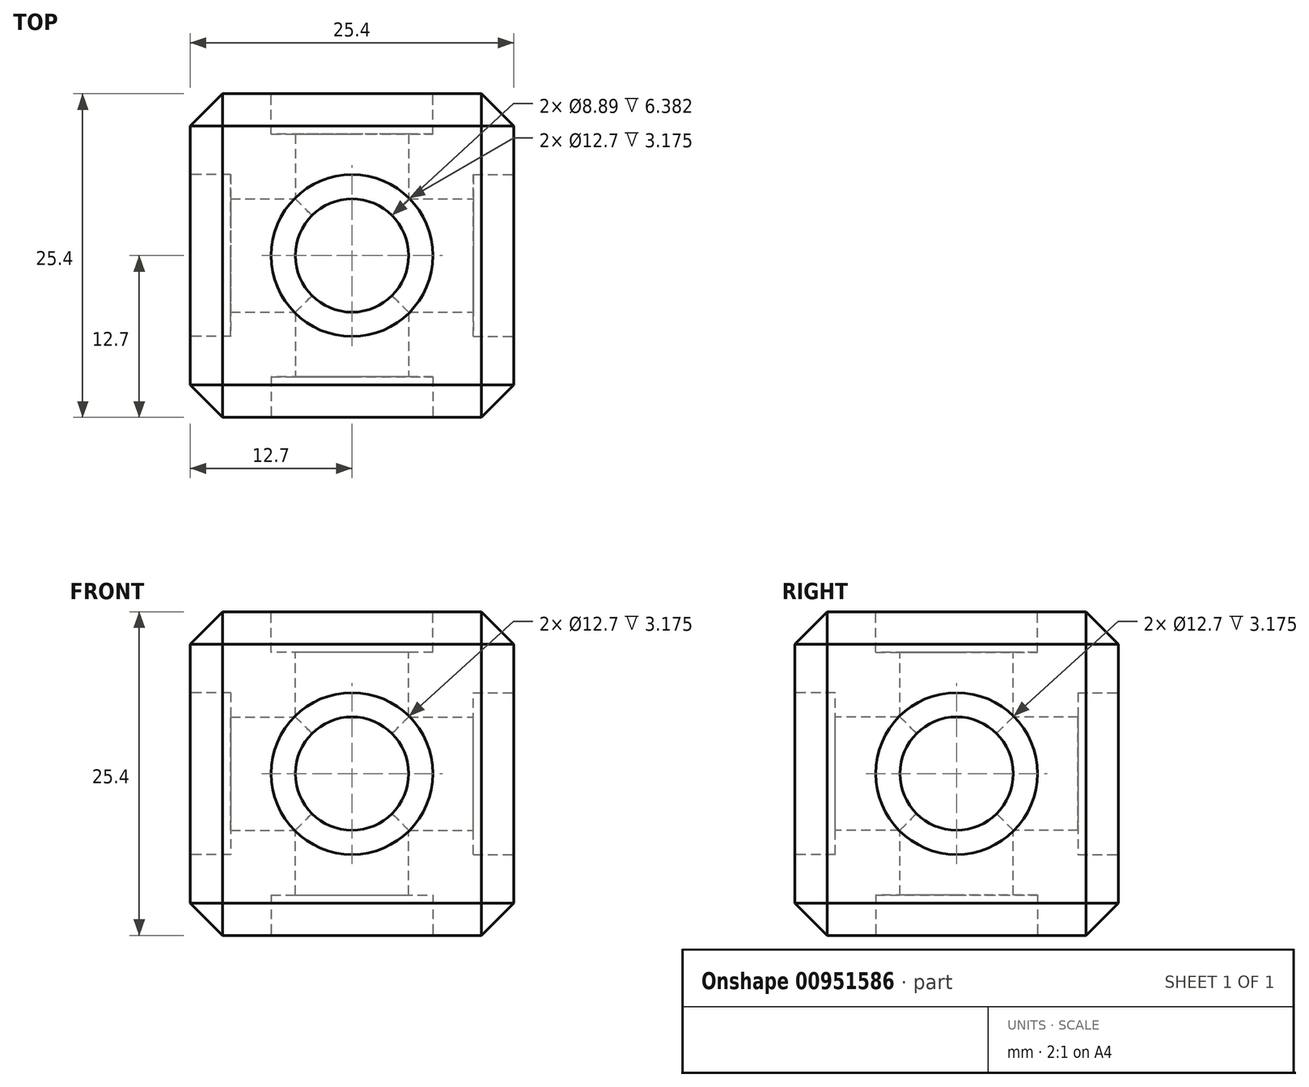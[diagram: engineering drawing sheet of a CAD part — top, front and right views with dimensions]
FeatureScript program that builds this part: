
annotation { "Feature Type Name" : "Feature", "Feature Type Description" : "" }
export const myFeature = defineFeature(function(context is Context, id is Id, definition is map)
    precondition{}
    {
        {
            var Q0;
            Q0=qCreatedBy(makeId("Front.planeOp"),FACE);
            var sketch = newSketch(context, id + "F0", { "sketchPlane" : qUnion([Q0])});
            skLineSegment(sketch, "E0.bottom", {"start": v(12.7, -12.7) * mm, "end": v(-12.7, -12.7) * mm});
            skLineSegment(sketch, "E0.top", {"start": v(12.7, 12.7) * mm, "end": v(-12.7, 12.7) * mm});
            skLineSegment(sketch, "E0.left", {"start": v(12.7, -12.7) * mm, "end": v(12.7, 12.7) * mm});
            skLineSegment(sketch, "E0.right", {"start": v(-12.7, -12.7) * mm, "end": v(-12.7, 12.7) * mm});
            skPoint(sketch, "E0.middle", {"position": v(0, 0) * mm});
            skSolve(sketch);
        }
        {
            var Q0;
            Q0 = qSketchRegion(id + "F0", true);
            extrude(context, id + "F1", {"entities" : qUnion([Q0]), "depth" : 12.7 * mm, "offsetDistance" : 25.4 * mm, "hasSecondDirection" : true, "secondDirectionOppositeDirection" : true, "secondDirectionDepth" : 12.7 * mm});
        }
        {
            var Q0;
            Q0=makeQuery(id+"F1.opExtrude","SWEPT_FACE",FACE,{"disambiguationData":[OSD([sQuery(id+"F0.wireOp",EDGE,"E0.top")])]});
            var sketch = newSketch(context, id + "F2", { "sketchPlane" : qUnion([Q0])});
            skCircle(sketch, "E1", {"center": v(0, 0) * mm, "radius": 6.35 * mm});
            skCircle(sketch, "E2", {"center": v(0, 0) * mm, "radius": 4.45 * mm});
            skSolve(sketch);
        }
        {
            var Q0;
            Q0=makeQuery(id+"F1.opExtrude","SWEPT_FACE",FACE,{"disambiguationData":[OSD([sQuery(id+"F0.wireOp",EDGE,"E0.bottom")])]});
            var sketch = newSketch(context, id + "F3", { "sketchPlane" : qUnion([Q0])});
            skCircle(sketch, "E3", {"center": v(0, 0) * mm, "radius": 6.35 * mm});
            skCircle(sketch, "E4", {"center": v(0, 0) * mm, "radius": 4.45 * mm});
            skSolve(sketch);
        }
        {
            var Q0;
            Q0=makeQuery(id+"F1.opExtrude","CAP_FACE",FACE,{"disambiguationData":[OSD([sQuery(id+"F0.wireOp",EDGE,"E0.bottom"),sQuery(id+"F0.wireOp",EDGE,"E0.top"),sQuery(id+"F0.wireOp",EDGE,"E0.left"),sQuery(id+"F0.wireOp",EDGE,"E0.right")])],"isStart":false});
            var sketch = newSketch(context, id + "F4", { "sketchPlane" : qUnion([Q0])});
            skCircle(sketch, "E5", {"center": v(0, 0) * mm, "radius": 6.35 * mm});
            skCircle(sketch, "E6", {"center": v(0, 0) * mm, "radius": 4.45 * mm});
            skSolve(sketch);
        }
        {
            var Q0;
            Q0=makeQuery(id+"F1.opExtrude","CAP_FACE",FACE,{"disambiguationData":[OSD([sQuery(id+"F0.wireOp",EDGE,"E0.bottom"),sQuery(id+"F0.wireOp",EDGE,"E0.top"),sQuery(id+"F0.wireOp",EDGE,"E0.left"),sQuery(id+"F0.wireOp",EDGE,"E0.right")])],"isStart":true});
            var sketch = newSketch(context, id + "F5", { "sketchPlane" : qUnion([Q0])});
            skCircle(sketch, "E7", {"center": v(0, 0) * mm, "radius": 6.35 * mm});
            skCircle(sketch, "E8", {"center": v(0, 0) * mm, "radius": 4.45 * mm});
            skSolve(sketch);
        }
        {
            var Q0;
            Q0=makeQuery(id+"F1.opExtrude","SWEPT_FACE",FACE,{"disambiguationData":[OSD([sQuery(id+"F0.wireOp",EDGE,"E0.left")])]});
            var sketch = newSketch(context, id + "F6", { "sketchPlane" : qUnion([Q0])});
            skCircle(sketch, "E9", {"center": v(0, 0) * mm, "radius": 6.35 * mm});
            skCircle(sketch, "E10", {"center": v(0, 0) * mm, "radius": 4.45 * mm});
            skSolve(sketch);
        }
        {
            var Q0;
            Q0=makeQuery(id+"F1.opExtrude","SWEPT_FACE",FACE,{"disambiguationData":[OSD([sQuery(id+"F0.wireOp",EDGE,"E0.right")])]});
            var sketch = newSketch(context, id + "F7", { "sketchPlane" : qUnion([Q0])});
            skCircle(sketch, "E11", {"center": v(0, 0) * mm, "radius": 6.35 * mm});
            skCircle(sketch, "E12", {"center": v(0, 0) * mm, "radius": 4.45 * mm});
            skSolve(sketch);
        }
        {
            var Q0;
            Q0=makeQuery(id+"F2.imprint","IMPRINT",FACE,{"disambiguationData":[TD([[makeQuery(id+"F2.imprint","IMPRINT",EDGE,{"derivedFrom":sQuery(id+"F2.wireOp",EDGE,"E2")}),1.0]])]});
            extrude(context, id + "F8", {"entities" : qUnion([Q0]), "operationType" : NewBodyOperationType.REMOVE, "oppositeDirection" : true, "depth" : 25.4 * mm, "offsetDistance" : 25.4 * mm});
        }
        {
            var Q0;
            Q0=makeQuery(id+"F4.imprint","IMPRINT",FACE,{"disambiguationData":[TD([[makeQuery(id+"F4.imprint","IMPRINT",EDGE,{"derivedFrom":sQuery(id+"F4.wireOp",EDGE,"E6")}),1.0]])]});
            extrude(context, id + "F9", {"entities" : qUnion([Q0]), "operationType" : NewBodyOperationType.REMOVE, "oppositeDirection" : true, "depth" : 25.4 * mm, "offsetDistance" : 25.4 * mm});
        }
        {
            var Q0;
            Q0=makeQuery(id+"F6.imprint","IMPRINT",FACE,{"disambiguationData":[TD([[makeQuery(id+"F6.imprint","IMPRINT",EDGE,{"derivedFrom":sQuery(id+"F6.wireOp",EDGE,"E10")}),1.0]])]});
            extrude(context, id + "F10", {"entities" : qUnion([Q0]), "operationType" : NewBodyOperationType.REMOVE, "oppositeDirection" : true, "depth" : 25.4 * mm, "offsetDistance" : 25.4 * mm});
        }
        {
            var Q0;
            Q0=makeQuery(id+"F2.imprint","IMPRINT",FACE,{"disambiguationData":[TD([[makeQuery(id+"F2.imprint","IMPRINT",EDGE,{"derivedFrom":sQuery(id+"F2.wireOp",EDGE,"E1")}),1.0]])]});
            extrude(context, id + "F11", {"entities" : qUnion([Q0]), "operationType" : NewBodyOperationType.REMOVE, "oppositeDirection" : true, "depth" : 3.17 * mm, "offsetDistance" : 25.4 * mm});
        }
        {
            var Q0;
            Q0=makeQuery(id+"F3.imprint","IMPRINT",FACE,{"disambiguationData":[TD([[makeQuery(id+"F3.imprint","IMPRINT",EDGE,{"derivedFrom":sQuery(id+"F3.wireOp",EDGE,"E3")}),1.0]])]});
            extrude(context, id + "F12", {"entities" : qUnion([Q0]), "operationType" : NewBodyOperationType.REMOVE, "oppositeDirection" : true, "depth" : 3.17 * mm, "offsetDistance" : 25.4 * mm});
        }
        {
            var Q0;
            Q0=makeQuery(id+"F4.imprint","IMPRINT",FACE,{"disambiguationData":[TD([[makeQuery(id+"F4.imprint","IMPRINT",EDGE,{"derivedFrom":sQuery(id+"F4.wireOp",EDGE,"E5")}),1.0]])]});
            extrude(context, id + "F13", {"entities" : qUnion([Q0]), "operationType" : NewBodyOperationType.REMOVE, "oppositeDirection" : true, "depth" : 3.17 * mm, "offsetDistance" : 25.4 * mm});
        }
        {
            var Q0;
            Q0=makeQuery(id+"F5.imprint","IMPRINT",FACE,{"disambiguationData":[TD([[makeQuery(id+"F5.imprint","IMPRINT",EDGE,{"derivedFrom":sQuery(id+"F5.wireOp",EDGE,"E7")}),1.0]])]});
            extrude(context, id + "F14", {"entities" : qUnion([Q0]), "operationType" : NewBodyOperationType.REMOVE, "oppositeDirection" : true, "depth" : 3.17 * mm, "offsetDistance" : 25.4 * mm});
        }
        {
            var Q0;
            Q0=makeQuery(id+"F6.imprint","IMPRINT",FACE,{"disambiguationData":[TD([[makeQuery(id+"F6.imprint","IMPRINT",EDGE,{"derivedFrom":sQuery(id+"F6.wireOp",EDGE,"E9")}),1.0]])]});
            extrude(context, id + "F15", {"entities" : qUnion([Q0]), "operationType" : NewBodyOperationType.REMOVE, "oppositeDirection" : true, "depth" : 3.17 * mm, "offsetDistance" : 25.4 * mm});
        }
        {
            var Q0;
            Q0=makeQuery(id+"F7.imprint","IMPRINT",FACE,{"disambiguationData":[TD([[makeQuery(id+"F7.imprint","IMPRINT",EDGE,{"derivedFrom":sQuery(id+"F7.wireOp",EDGE,"E11")}),1.0]])]});
            extrude(context, id + "F16", {"entities" : qUnion([Q0]), "operationType" : NewBodyOperationType.REMOVE, "oppositeDirection" : true, "depth" : 3.17 * mm, "offsetDistance" : 25.4 * mm});
        }
        {
            var Q0;
            Q0=makeQuery(id+"F1.opExtrude","CAP_EDGE",EDGE,{"disambiguationData":[OSD([sQuery(id+"F0.wireOp",EDGE,"E0.left")])],"isStart":false});
            var Q1;
            Q1=makeQuery(id+"F1.opExtrude","CAP_EDGE",EDGE,{"disambiguationData":[OSD([sQuery(id+"F0.wireOp",EDGE,"E0.bottom")])],"isStart":false});
            var Q2;
            Q2=makeQuery(id+"F1.opExtrude","CAP_EDGE",EDGE,{"disambiguationData":[OSD([sQuery(id+"F0.wireOp",EDGE,"E0.right")])],"isStart":false});
            var Q3;
            Q3=makeQuery(id+"F1.opExtrude","CAP_EDGE",EDGE,{"disambiguationData":[OSD([sQuery(id+"F0.wireOp",EDGE,"E0.top")])],"isStart":false});
            var Q4;
            Q4=makeQuery(id+"F1.opExtrude","SWEPT_EDGE",EDGE,{"disambiguationData":[OSD([sQuery(id+"F0.wireOp",EDGE,"E0.bottom"),sQuery(id+"F0.wireOp",EDGE,"E0.left")])]});
            var Q5;
            Q5=makeQuery(id+"F1.opExtrude","SWEPT_EDGE",EDGE,{"disambiguationData":[OSD([sQuery(id+"F0.wireOp",EDGE,"E0.bottom"),sQuery(id+"F0.wireOp",EDGE,"E0.right")])]});
            var Q6;
            Q6=makeQuery(id+"F1.opExtrude","CAP_EDGE",EDGE,{"disambiguationData":[OSD([sQuery(id+"F0.wireOp",EDGE,"E0.bottom")])],"isStart":true});
            var Q7;
            Q7=makeQuery(id+"F1.opExtrude","CAP_EDGE",EDGE,{"disambiguationData":[OSD([sQuery(id+"F0.wireOp",EDGE,"E0.left")])],"isStart":true});
            var Q8;
            Q8=makeQuery(id+"F1.opExtrude","SWEPT_EDGE",EDGE,{"disambiguationData":[OSD([sQuery(id+"F0.wireOp",EDGE,"E0.top"),sQuery(id+"F0.wireOp",EDGE,"E0.left")])]});
            var Q9;
            Q9=makeQuery(id+"F1.opExtrude","CAP_EDGE",EDGE,{"disambiguationData":[OSD([sQuery(id+"F0.wireOp",EDGE,"E0.top")])],"isStart":true});
            var Q10;
            Q10=makeQuery(id+"F1.opExtrude","SWEPT_EDGE",EDGE,{"disambiguationData":[OSD([sQuery(id+"F0.wireOp",EDGE,"E0.top"),sQuery(id+"F0.wireOp",EDGE,"E0.right")])]});
            var Q11;
            Q11=makeQuery(id+"F1.opExtrude","CAP_EDGE",EDGE,{"disambiguationData":[OSD([sQuery(id+"F0.wireOp",EDGE,"E0.right")])],"isStart":true});
            chamfer(context, id + "F17", {"entities" : qUnion([Q0, Q1, Q2, Q3, Q4, Q5, Q6, Q7, Q8, Q9, Q10, Q11]), "width" : 2.54 * mm, "tangentPropagation" : true});
        }
    });
